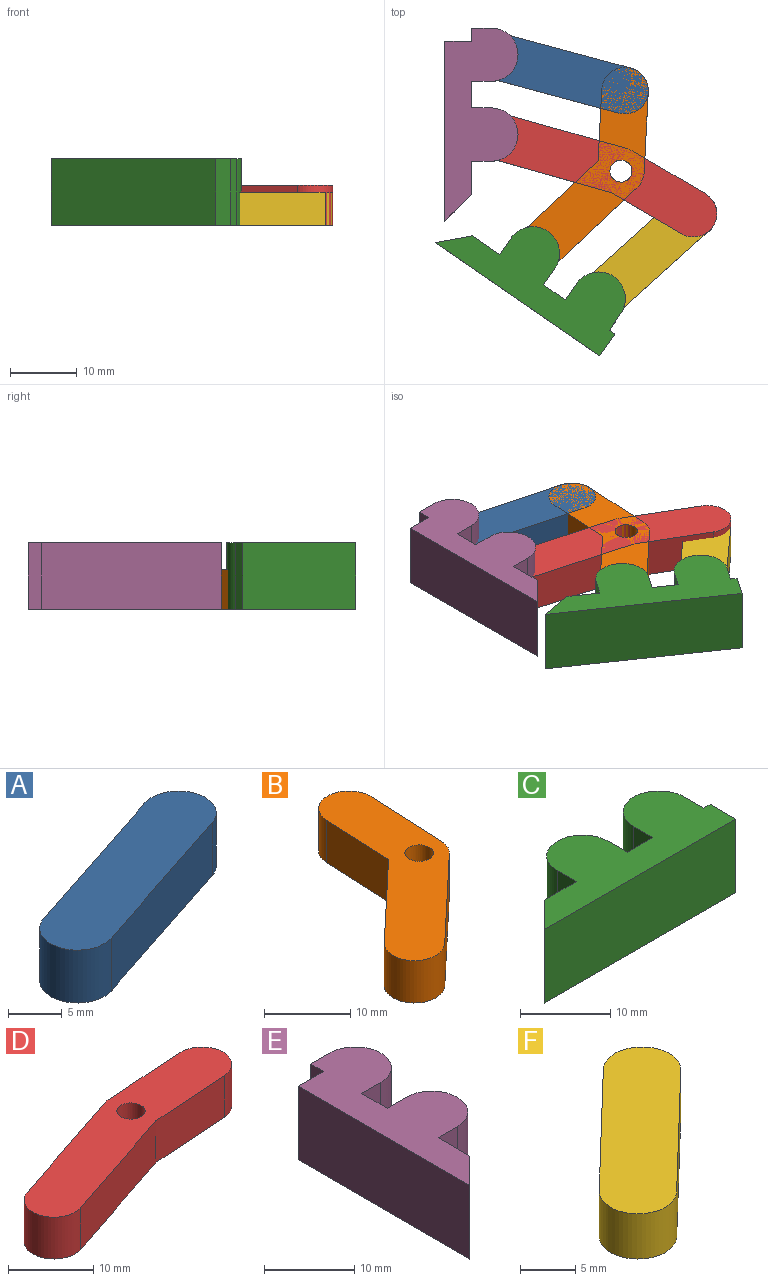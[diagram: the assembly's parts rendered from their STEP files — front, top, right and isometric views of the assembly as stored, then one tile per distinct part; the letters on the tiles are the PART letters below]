
ASSEMBLY  parts=6 mates=7
PART A: 6 faces, bbox 26.7x13.5x6 mm
  f0: plane 19.74x6.49mm, normal (-0.31,0.95,0), area 124.7mm2, adj f1,f3,f4,f5
  f1: cylinder r=3.5mm len=6.83mm, axis (0,0,-1), area 66mm2, adj f0,f2,f4,f5
  f2: plane 19.74x6.49mm, normal (0.31,-0.95,0), area 124.7mm2, adj f1,f3,f4,f5
  f3: cylinder r=3.5mm len=6.83mm, axis (0,0,-1), area 66mm2, adj f0,f2,f4,f5
  f4: plane 26.74x13.49mm, normal (0,0,1), area 183.9mm2, adj f0,f1,f2,f3
  f5: plane 26.74x13.49mm, normal (0,0,-1), area 183.9mm2, adj f0,f1,f2,f3
PART B: 10 faces, bbox 20.7x31.5x6 mm
  f0: plane 12.14x11.43mm, normal (-0.69,0.73,0), area 100mm2, adj f1,f6,f8,f9
  f1: cylinder r=3.5mm len=6.05mm, axis (0,0,-1), area 66mm2, adj f0,f2,f8,f9
  f2: plane 13.16x12.4mm, normal (0.69,-0.73,0), area 108.5mm2, adj f1,f3,f8,f9
  f3: cylinder r=3.5mm len=6mm, axis (0,0,-1), area 16.1mm2, adj f2,f4,f8,f9
  f4: plane 12.08x6mm, normal (1,-0.05,0), area 72.6mm2, adj f3,f5,f8,f9
  f5: cylinder r=3.5mm len=7mm, axis (0,0,-1), area 66mm2, adj f4,f6,f8,f9
  f6: plane 10.67x6mm, normal (-1,0.05,0), area 64.1mm2, adj f0,f5,f8,f9
  f7: cylinder r=1.65mm len=6mm, axis (0,0,-1), area 62.2mm2, adj f8,f9
  f8: plane 31.49x20.74mm, normal (0,0,1), area 241mm2, adj f0,f1,f2,f3,f4,f5,f6,f7
  f9: plane 31.49x20.74mm, normal (0,0,-1), area 241mm2, adj f0,f1,f2,f3,f4,f5,f6,f7
PART C: 14 faces, bbox 30x11x10 mm
  f0: cylinder r=4mm len=10mm, axis (0,0,-1), area 125.7mm2, adj f1,f11,f12,f13
  f1: plane 10x3mm, normal (-1,0,0), area 30mm2, adj f0,f2,f12,f13
  f2: plane 10x4mm, normal (0,1,0), area 40mm2, adj f1,f3,f12,f13
  f3: plane 10x3mm, normal (1,0,0), area 30mm2, adj f2,f4,f12,f13
  f4: cylinder r=4mm len=10mm, axis (0,0,-1), area 125.7mm2, adj f3,f5,f12,f13
  f5: plane 10x3mm, normal (-1,0,0), area 30mm2, adj f4,f6,f12,f13
  f6: plane 10x5mm, normal (0,1,0), area 50mm2, adj f5,f7,f12,f13
  f7: plane 10x4mm, normal (-0.71,0.71,0), area 56.6mm2, adj f6,f8,f12,f13
  f8: plane 30x10mm, normal (0,-1,0), area 300mm2, adj f7,f9,f12,f13
  f9: plane 10x4mm, normal (1,0,0), area 40mm2, adj f8,f10,f12,f13
  f10: plane 10x1mm, normal (0,1,0), area 10mm2, adj f9,f11,f12,f13
  f11: plane 10x3mm, normal (1,0,0), area 30mm2, adj f0,f10,f12,f13
  f12: plane 30x11mm, normal (0,0,1), area 210.3mm2, adj f0,f1,f2,f3,f4,f5,f6,f7
  f13: plane 30x11mm, normal (0,0,-1), area 210.3mm2, adj f0,f1,f2,f3,f4,f5,f6,f7
PART D: 10 faces, bbox 38.8x14.2x6 mm
  f0: plane 18.74x6.26mm, normal (0.32,-0.95,0), area 118.5mm2, adj f1,f6,f8,f9
  f1: plane 12.17x6mm, normal (0.07,-1,0), area 73.2mm2, adj f0,f2,f8,f9
  f2: cylinder r=3.5mm len=6.99mm, axis (0,0,-1), area 66mm2, adj f1,f3,f8,f9
  f3: plane 12.62x6mm, normal (-0.07,1,0), area 75.9mm2, adj f2,f4,f8,f9
  f4: cylinder r=3.5mm len=6mm, axis (0,0,-1), area 5.4mm2, adj f3,f5,f8,f9
  f5: plane 19.16x6.4mm, normal (-0.32,0.95,0), area 121.2mm2, adj f4,f6,f8,f9
  f6: cylinder r=3.5mm len=6.82mm, axis (0,0,-1), area 66mm2, adj f0,f5,f8,f9
  f7: cylinder r=1.65mm len=6mm, axis (0,0,-1), area 62.2mm2, adj f8,f9
  f8: plane 38.78x14.24mm, normal (0,0,1), area 259.9mm2, adj f0,f1,f2,f3,f4,f5,f6,f7
  f9: plane 38.78x14.24mm, normal (0,0,-1), area 259.9mm2, adj f0,f1,f2,f3,f4,f5,f6,f7
PART E: 14 faces, bbox 11x29x10 mm
  f0: plane 10x3mm, normal (0,1,0), area 30mm2, adj f1,f11,f12,f13
  f1: plane 10x4mm, normal (1,0,0), area 40mm2, adj f0,f2,f12,f13
  f2: plane 10x3mm, normal (0,-1,0), area 30mm2, adj f1,f3,f12,f13
  f3: cylinder r=4mm len=10mm, axis (0,0,-1), area 125.7mm2, adj f2,f4,f12,f13
  f4: plane 10x3mm, normal (0,1,0), area 30mm2, adj f3,f5,f12,f13
  f5: plane 10x2mm, normal (-1,0,0), area 20mm2, adj f4,f6,f12,f13
  f6: plane 10x4mm, normal (0,1,0), area 40mm2, adj f5,f7,f12,f13
  f7: plane 27x10mm, normal (-1,0,0), area 270mm2, adj f6,f8,f12,f13
  f8: plane 10x4mm, normal (0.71,-0.71,0), area 56.6mm2, adj f7,f9,f12,f13
  f9: plane 10x5mm, normal (1,0,0), area 50mm2, adj f8,f10,f12,f13
  f10: plane 10x3mm, normal (0,-1,0), area 30mm2, adj f9,f11,f12,f13
  f11: cylinder r=4mm len=10mm, axis (0,0,-1), area 125.7mm2, adj f0,f10,f12,f13
  f12: plane 29x11mm, normal (0,0,1), area 198.3mm2, adj f0,f1,f2,f3,f4,f5,f6,f7
  f13: plane 29x11mm, normal (0,0,-1), area 198.3mm2, adj f0,f1,f2,f3,f4,f5,f6,f7
PART F: 6 faces, bbox 20.8x20.2x5 mm
  f0: plane 13.78x13.24mm, normal (0.69,-0.72,0), area 95.6mm2, adj f1,f3,f4,f5
  f1: cylinder r=3.5mm len=6.02mm, axis (0,0,-1), area 55mm2, adj f0,f2,f4,f5
  f2: plane 13.78x13.24mm, normal (-0.69,0.72,0), area 95.6mm2, adj f1,f3,f4,f5
  f3: cylinder r=3.5mm len=6.02mm, axis (0,0,-1), area 55mm2, adj f0,f2,f4,f5
  f4: plane 20.78x20.24mm, normal (0,0,1), area 172.3mm2, adj f0,f1,f2,f3
  f5: plane 20.78x20.24mm, normal (0,0,-1), area 172.3mm2, adj f0,f1,f2,f3
PLACE A rot(axis=(0,0,-1),33.2deg) t=(-22.08,-3.03,5.23)mm
PLACE B rot(axis=(0,0,-1),0.2deg) t=(-7.67,-23.24,5.23)mm
PLACE C rot(axis=(0,0,-1),34.5deg) t=(-11.01,-14.16,5.23)mm
PLACE D rot(axis=(0,0,-1),34.2deg) t=(-15.66,-4.75,5.23)mm
PLACE E t=(-7.87,-11.45,5.23)mm fixed
PLACE F rot(axis=(0,0,-1),2deg) t=(-10.08,-29.22,5.23)mm
MATE revolute D.f4 <-> B.f3  axis (0,0,-1) through (18.57,-0.93,5.23)mm
MATE revolute A.f1 <-> E.f3  axis (0,0,-1) through (-0.87,16.55,5.23)mm
MATE revolute D.f6 <-> E.f11  axis (0,0,-1) through (-0.87,4.55,5.23)mm
MATE revolute B.f5 <-> A.f3  axis (0,0,-1) through (19.19,11.15,5.23)mm
MATE revolute F.f1 <-> D.f2  axis (0,0,-1) through (29.48,-7.33,5.23)mm
MATE revolute C.f4 <-> B.f1  axis (0,0,-1) through (5.37,-13.29,5.23)mm
MATE revolute F.f3 <-> C.f0  axis (0,0,-1) through (15.25,-20.09,5.23)mm
